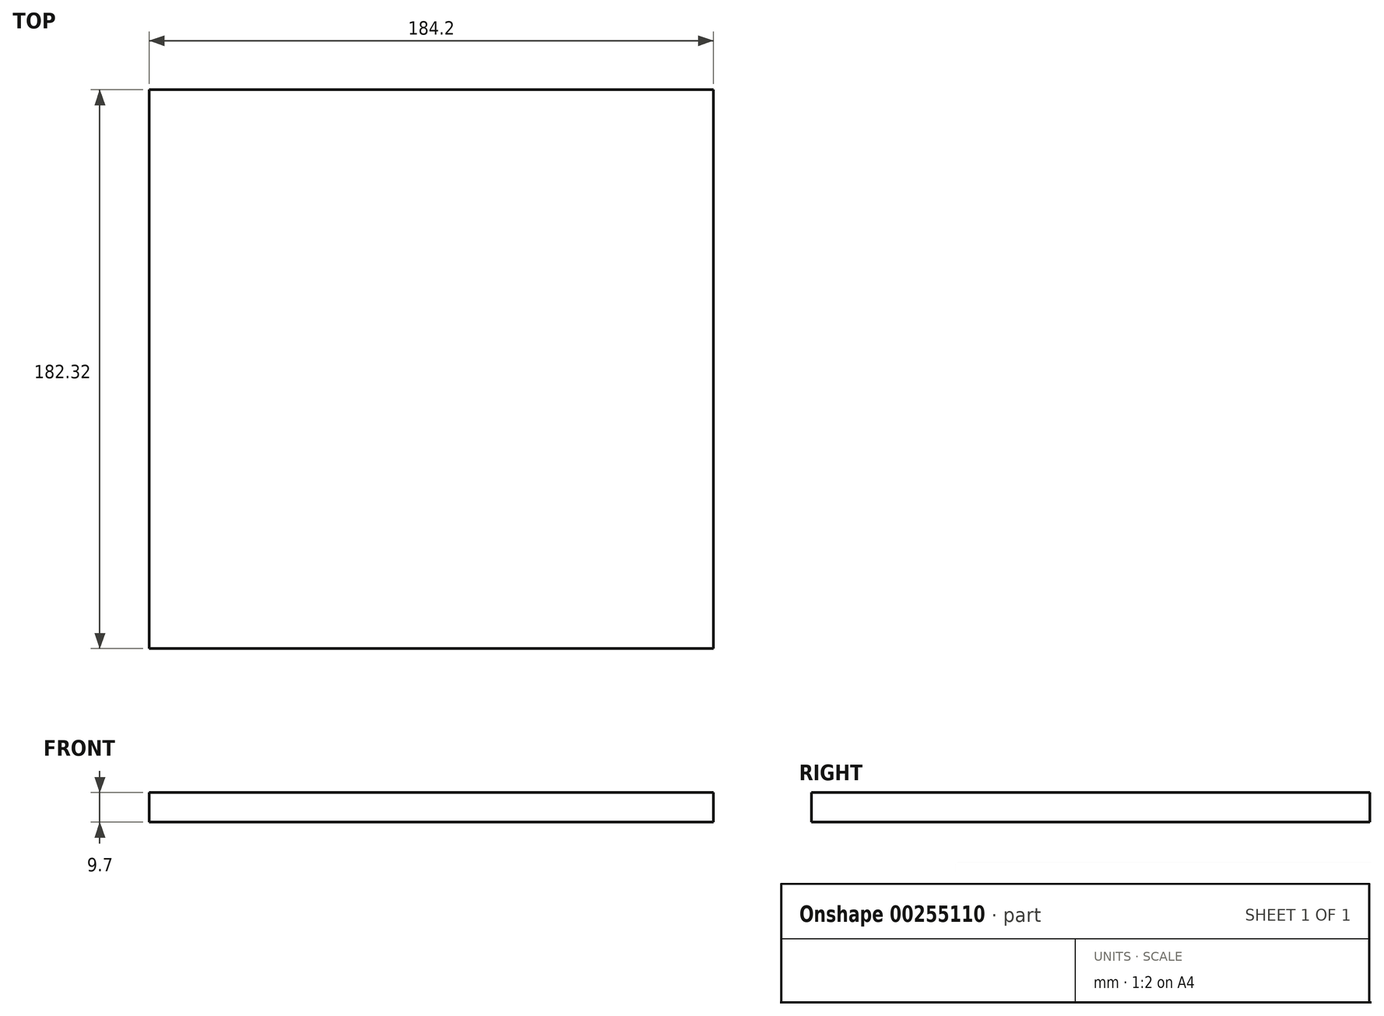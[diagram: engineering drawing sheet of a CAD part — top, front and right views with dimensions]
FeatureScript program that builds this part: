
annotation { "Feature Type Name" : "Feature", "Feature Type Description" : "" }
export const myFeature = defineFeature(function(context is Context, id is Id, definition is map)
    precondition{}
    {
        {
            var Q0;
            Q0=qCreatedBy(makeId("Top.planeOp"),FACE);
            var sketch = newSketch(context, id + "F0", { "sketchPlane" : qUnion([Q0])});
            skLineSegment(sketch, "E0.bottom", {"start": v(92.1, -91.16) * mm, "end": v(-92.1, -91.16) * mm});
            skLineSegment(sketch, "E0.top", {"start": v(92.1, 91.16) * mm, "end": v(-92.1, 91.16) * mm});
            skLineSegment(sketch, "E0.left", {"start": v(92.1, -91.16) * mm, "end": v(92.1, 91.16) * mm});
            skLineSegment(sketch, "E0.right", {"start": v(-92.1, -91.16) * mm, "end": v(-92.1, 91.16) * mm});
            skPoint(sketch, "E0.middle", {"position": v(0, 0) * mm});
            skSolve(sketch);
        }
        {
            var Q0;
            Q0 = qSketchRegion(id + "F0", true);
            extrude(context, id + "F1", {"entities" : qUnion([Q0]), "depth" : 9.7 * mm});
        }
    });
